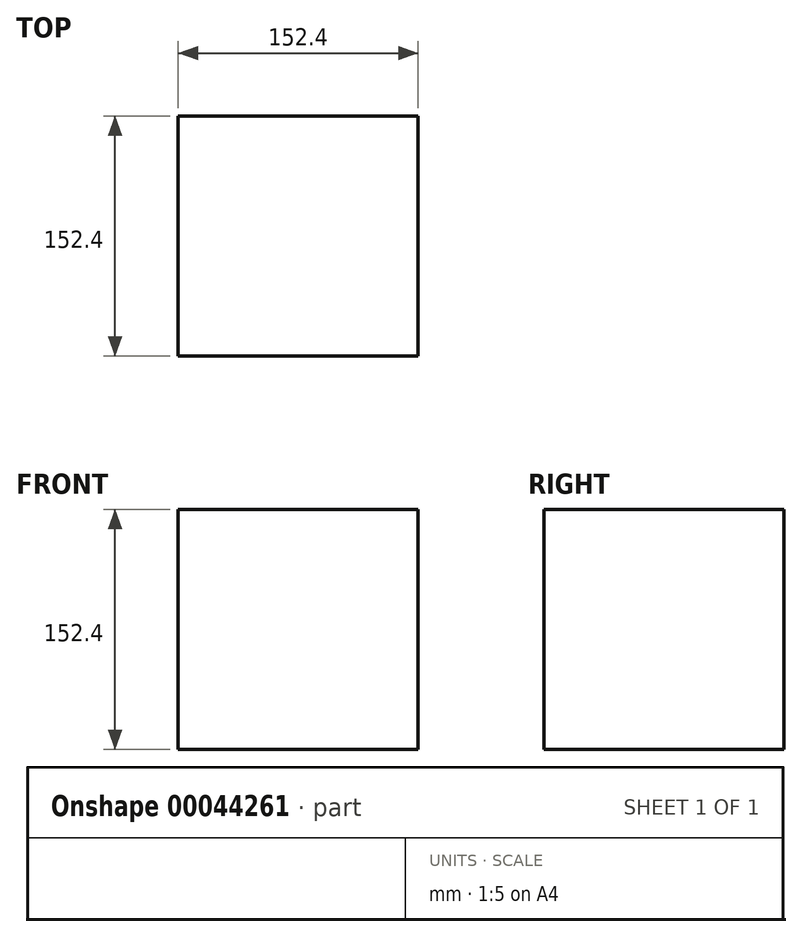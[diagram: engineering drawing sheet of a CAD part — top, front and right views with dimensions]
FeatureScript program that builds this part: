
annotation { "Feature Type Name" : "Feature", "Feature Type Description" : "" }
export const myFeature = defineFeature(function(context is Context, id is Id, definition is map)
    precondition{}
    {
        {
            var Q0;
            Q0=qCreatedBy(makeId("Top.planeOp"),FACE);
            var sketch = newSketch(context, id + "F0", { "sketchPlane" : qUnion([Q0])});
            skLineSegment(sketch, "E0.bottom", {"start": v(-76.08, -75.33) * mm, "end": v(76.32, -75.33) * mm});
            skLineSegment(sketch, "E0.top", {"start": v(-76.08, 77.07) * mm, "end": v(76.32, 77.07) * mm});
            skLineSegment(sketch, "E0.left", {"start": v(-76.08, -75.33) * mm, "end": v(-76.08, 77.07) * mm});
            skLineSegment(sketch, "E0.right", {"start": v(76.32, -75.33) * mm, "end": v(76.32, 77.07) * mm});
            skSolve(sketch);
        }
        {
            var Q0;
            Q0 = qSketchRegion(id + "F0", true);
            extrude(context, id + "F1", {"entities" : qUnion([Q0]), "depth" : 152.4 * mm});
        }
    });
